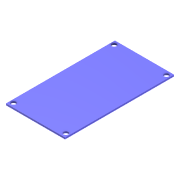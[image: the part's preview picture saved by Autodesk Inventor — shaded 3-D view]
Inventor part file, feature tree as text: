
AUTODESK INVENTOR PART (.ipt)
format: ipt  version: 2022 (Build 260153000, 153)  size: 111,104 bytes
history: native  units: mm
features: sketch x2, extrude x1, hole x1, projected_geometry x1
ambient origin geometry x8: Origin, YZ Plane, XZ Plane, XY Plane, X Axis, Y Axis, Z Axis, Center Point
bodies: Solid1 (feature_tree)
feature tree (5):
  extrude  "Extrusion1"  Depth=66.5mm
  hole  "Hole1"  [1 undecoded]
  sketch  "Sketch1"  dims[d0=36.0mm d1=66.5mm]
  sketch  "Sketch2"  dims[d2=1.0mm d3=0.0mm d11=3.0mm d12=3.0mm d13=3.0mm d14=3.0mm d17=0.5mm d18=1.0mm d19=3.0mm d20=6.0mm d21=4.0mm d22=2.0mm d23=90.0deg d24=6.0mm d25=0.0mm]
  projected_geometry  "Project Cut Edges1"
note: 1 required parameter value undecoded (feature->parameter linkage not recoverable at this tier; creation-order binding heuristic only, values carry confidence <= 0.55)
